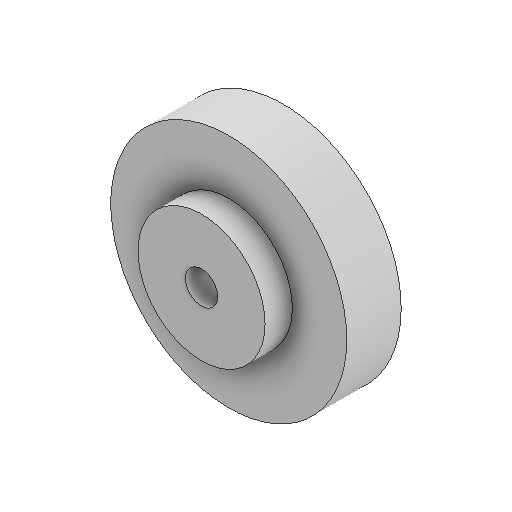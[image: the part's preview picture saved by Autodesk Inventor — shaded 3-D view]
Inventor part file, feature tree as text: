
AUTODESK INVENTOR PART (.ipt)
format: ipt  version: 2025.1 (Build 291241000, 241)  size: 124,928 bytes
history: native  units: mm
features: sketch x5, extrude x4, other x1, hole x1
ambient origin geometry x8: Origin, YZ Plane, XZ Plane, XY Plane, X Axis, Y Axis, Z Axis, Center Point
bodies: Body1 (feature_tree)
feature tree (11):
  other  "Bryła1"
  extrude  "Wyciągnięcie proste1"  Depth=13.0mm
  extrude  "Wyciągnięcie proste2"  Depth=1.5mm TaperAngle=0.0deg
  extrude  "Wyciągnięcie proste3"  Depth=7.0mm
  extrude  "Wyciągnięcie proste4"  Depth=1.5mm TaperAngle=0.0deg
  hole  "Otwór1"  [1 undecoded]
  sketch  "Szkic1"
  sketch  "Szkic2"
  sketch  "Szkic3"
  sketch  "Szkic4"
  sketch  "Szkic5"
note: 1 required parameter value undecoded (feature->parameter linkage not recoverable at this tier; creation-order binding heuristic only, values carry confidence <= 0.55)
